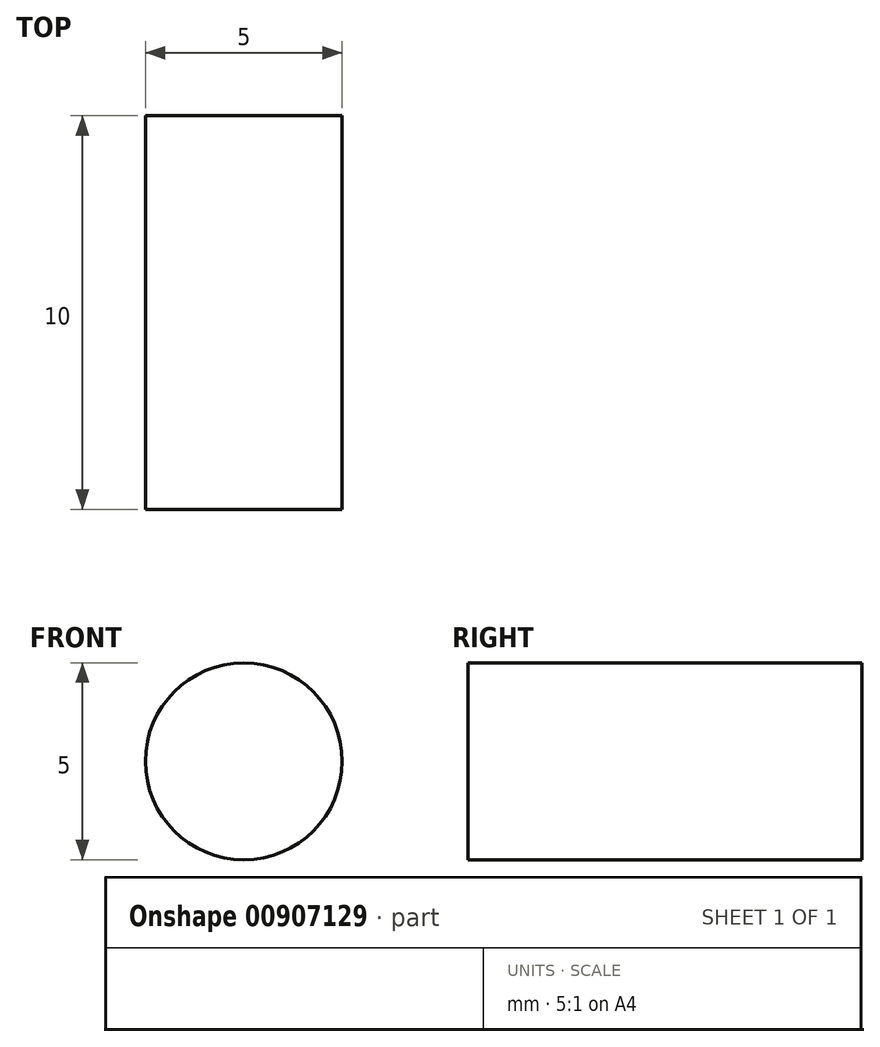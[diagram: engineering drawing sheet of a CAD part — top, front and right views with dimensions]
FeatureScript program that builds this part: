
annotation { "Feature Type Name" : "Feature", "Feature Type Description" : "" }
export const myFeature = defineFeature(function(context is Context, id is Id, definition is map)
    precondition{}
    {
        {
            var Q0;
            Q0=qCreatedBy(makeId("Front.planeOp"),FACE);
            var sketch = newSketch(context, id + "F0", { "sketchPlane" : qUnion([Q0])});
            skCircle(sketch, "E0", {"center": v(0, 0) * mm, "radius": 2.5 * mm});
            skSolve(sketch);
        }
        {
            var Q0;
            Q0=qSketchRegion(id+"F0",true);
            extrude(context, id + "F1", {"entities" : qUnion([Q0]), "endBound" : BoundingType.SYMMETRIC, "oppositeDirection" : true, "depth" : 10 * mm, "offsetDistance" : 25 * mm});
        }
    });
